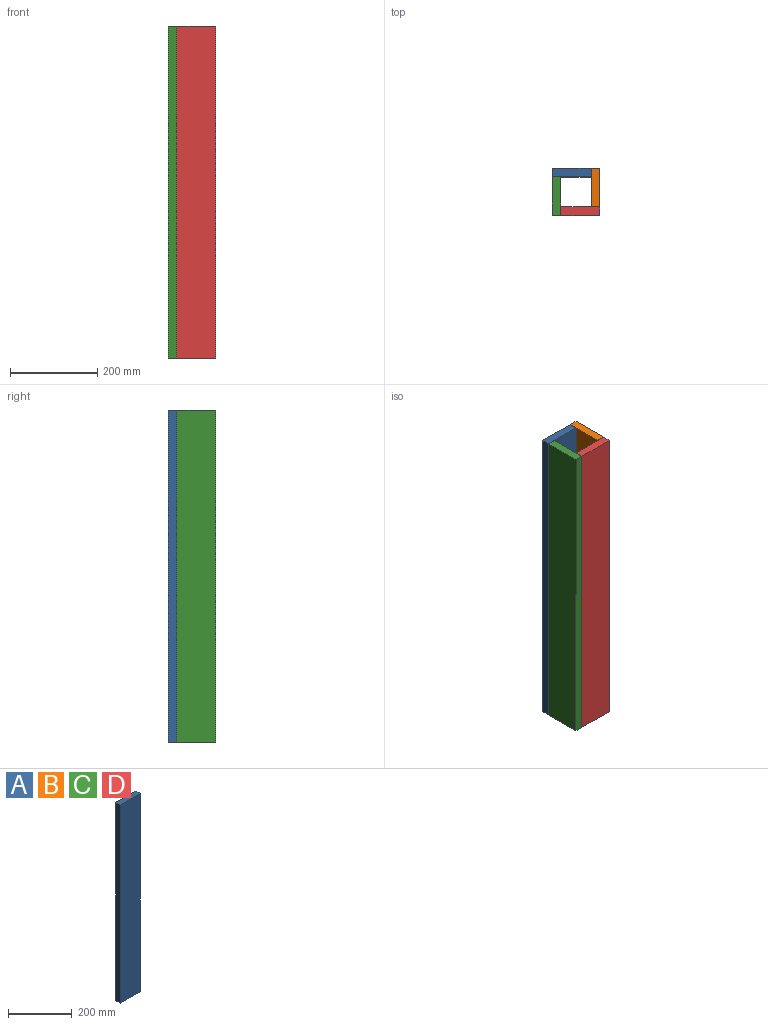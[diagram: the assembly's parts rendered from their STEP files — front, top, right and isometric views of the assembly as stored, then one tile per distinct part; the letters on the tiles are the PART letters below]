
ASSEMBLY  parts=4 mates=3
PART A: 6 faces, bbox 88.9x19.1x762 mm
  f0: plane 88.9x19.05mm, normal (0,0,1), area 1693.5mm2, adj f1,f3,f4,f5
  f1: plane 762x19.05mm, normal (-1,0,0), area 14516.1mm2, adj f0,f2,f4,f5
  f2: plane 88.9x19.05mm, normal (0,0,-1), area 1693.5mm2, adj f1,f3,f4,f5
  f3: plane 762x19.05mm, normal (1,0,0), area 14516.1mm2, adj f0,f2,f4,f5
  f4: plane 762x88.9mm, normal (0,-1,0), area 67741.8mm2, adj f0,f1,f2,f3
  f5: plane 762x88.9mm, normal (0,1,0), area 67741.8mm2, adj f0,f1,f2,f3
PART B: same geometry as A
PART C: same geometry as A
PART D: same geometry as A
PLACE A t=(-104.78,-201.5,65.06)mm
PLACE B rot(axis=(0,0,-1),90deg) t=(3.17,-201.5,65.06)mm
PLACE C rot(axis=(0,0,1),90deg) t=(-104.78,-309.45,65.06)mm
PLACE D rot(axis=(0,0,1),180deg) t=(3.17,-309.45,65.06)mm fixed
MATE fastened D.f3 <-> C.f4  axis (-1,0,0) through (-85.73,-309.45,65.06)mm
MATE fastened C.f3 <-> A.f4  axis (0,1,0) through (-104.78,-220.55,65.06)mm
MATE fastened B.f4 <-> A.f3  axis (-1,0,0) through (-15.88,-201.5,65.06)mm
